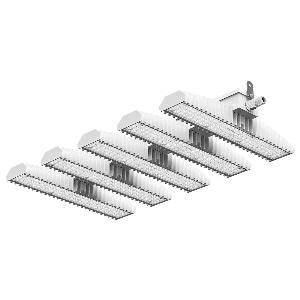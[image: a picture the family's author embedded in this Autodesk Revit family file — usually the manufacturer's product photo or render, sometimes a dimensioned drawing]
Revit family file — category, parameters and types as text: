
# Revit family: 3f_filippi_-_3f_lem_ho_medio_3f_filippi_-_58969_-_3f_lem_5_ho_led_350_cr_medio
name_source: partatom
category: Lighting Fixtures
units: mm (PartAtom-declared; Revit-internal decimal feet)

## family parameters
Cut with Voids When Loaded = No
Host = Face
Light Source = No
Part Type = Normal
Room Calculation Point = No
Round Connector Dimension = Use Diameter
Shared = No

## types (1)
- 3F Filippi - 3F LEM HO Medio (1 x LED, 55320 lm, 345 W, 4000 K)
    Apparent Load = 345 VA
    Approval mark = CE
    CIE Flux Codes = 83 96 99 100 100
    Color Rendering = 80
    Color Temperature = 4000 K
    Control Gear = Electronic ballast
    Default Elevation = 1800 mm
    Description = Industrial luminaire with high light output and high luminous efficiency designed with the most innovative technologies for environments with temperature up to 55°C.

ILLUMINOTECHNICAL
Luminous efficiency 100% (DLOR 100%, ULOR 0%).
Initial luminous flux of the luminaire 55320 lm.
Medium distribution with rectangular shape.
Installation Interdistance Transv.D = 1.02 x hu - Long.D = 1.06 x hu.
Tabular UGR (CIE 117 - 4H-8H; S=0.25H; 70/50/20): RUG 20.2 - 19.8.
Beam angle: 65° - 67°.
Luminous efficacy 160 lm/W.
Lifetime (L93/B10): 30000 h. (tq+25°C)
Lifetime (L90/B10): 50000 h. (tq+25°C)
Lifetime (L85/B10): 80000 h. (tq+25°C)
Lifetime (L80/B10): 100000 h. (tq+25°C)
Lifetime (L85/B10): 50000 h. (tq+55°C)
Sudden decreased luminous flux after 50000 hours: 0% (C0).
Photobiological safety in compliance with IEC/TR 62778: RG0 risk exempt, (IEC 62471).
In compliance with IEC/EN 62722-2-1 - IEC/EN 62717 standards.

SOURCE
5 Mid-Power linear LED modules 70W/840.
Energy efficiency class (UE 2019/2020 - UE 2019/2015): C.
CIE 13.3 Colour rendering index: CRI >80 (R9 <50%).
IES TM-30 Fidelity Index: Rf = 84 Rg = 95.
CCT nominal colour temperature 4000 K.
Colour initial tolerance (MacAdam): SDCM 3.

MECHANICAL
Passive modular heatsinks in die-casted aluminium, painted in white colour.
To optimize the thermal management of the LED module, the heatsinks are oversized and provided with self-cleaning of cooling fins.
Wiring body in aluminium and galvanised steel anchored solidly to the sinks and thermally separated.
3F Lens lenses with high luminous efficiency, transparent methacrylate (PMMA), fixed to the LED modules.
Fixing brackets in stainless steel.
Luminaire with limited surface temperature. - D - (EN 60598-2-24)
Dimensions: 952x542 mm, height 129 mm. Weight 21.655 kg.
IP65 protection degree.
Mechanical strength to impacts IK06 (1 joule).
Glow-wire test resistance 650°C.

ELECTRICAL
Halogen Free electronic wiring 230V-50/60Hz, power factor 0.97, THD <25%, constant output current, class I, 3 driver.
Power of the luminaire 345 W.
ENEC - CE.
SAFE FLICKER: PstLM=<1 and SVM=<0.4 (IEC TR 61547-1 and IEC TR 63158), to ensure a more comfortable and safe light.
Luminaire compliant with EN 60598-2-22 for power supply from a centralised emergency system CPSS (Central Power Supply System), not incorporated in the luminaire - high risk areas excluded. The default power and flux are 100% in AC and 100% in DC.
Ambient temperature from -30°C to +55°C.
Temperature class T6 max 85°C.
Quick connection via M20 3P connector with 9-13 mm tightening range.
Power unit positioned on a separate compartment by the LED module to ensure optimum temperatures of cabling components, to be inspectable and maintainable.
Relative humidity UR: <85%.

INSTALLATION
Ceiling / Suspended / Wall.
All accessories dedicated to this product are available on the Catalog and on our website www.3F-Filippi.com.

APPLICATIONS
In commercial environments, exhibition and industrial areas, stores, open areas.
Environments in which it is necessary a total protection against falling fragments (eg environments with foodstuffs or machines with moving parts or with extreme temperature changes), use luminaires with polycarbonate lenses.

WARNING
Fixture not suitable for cold stores with an ambient temperature <0°C and/or relative humidity >85%.
Luminaire designed for disposal/recycling at end-of-life.
Replaceable (LED only) light source by a professional. Replaceable control gear by a professional.
    Height = 129 mm
    Lamp = 1 x LED
    Lamp Light Flux = 55320 lm
    Lamp Power = 345 W
    Lamp count = 1
    Length = 952 mm
    Lifetime = 50000 h
    Luminous efficacy = 160 lm/W
    Manufacturer = 3F Filippi
    ModVariant = No
    Model = 3F Filippi - 58969 - 3F LEM 5 HO LED 350 CR MEDIO
    Mounting Place = Ceiling
    Mounting Type = Pendant
    Number of Poles = 1
    OnlyDefault = Yes
    Power Factor = 1
    Product Name = 3F Filippi - 3F LEM HO Medio
    Product group = pendant luminaire
    ProductGroupID = 9
    Protection Class = Protection class I
    Protection Degree = IP 65
    RLX_Detail_Level = 1
    RLX_Emergency_Light_Flux = 0 lm
    RLX_Emergency_Type = 0
    RLX_Emergency_Type_DB = No
    RlxData = <blob elided: 132113 chars, md5=fb51ad3b>
    Socket = socket
    Standby Power = 0 W
    System Light Flux = 55320 lm
    System Power = 345 W
    Type Comments = Product without accessories
    Type Image = 3f_filippi_-_lem_5.jpg
    URL = http://relux.com
    VarID = ---
    Voltage = 0 V
    Weight = 0.00 kg
    Width = 542 mm

## geometry (parser evidence)
native form markers: Blend x4, Sweep x12
no freeform markers — native parametric forms only
